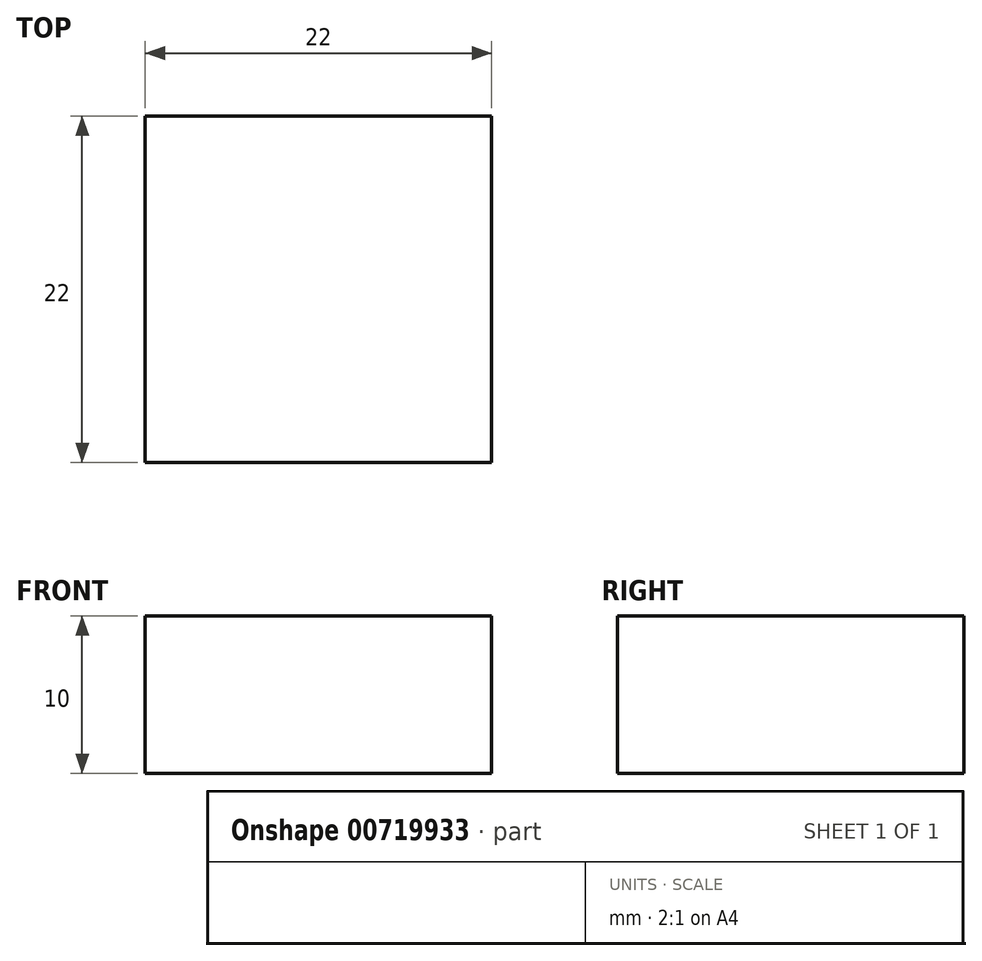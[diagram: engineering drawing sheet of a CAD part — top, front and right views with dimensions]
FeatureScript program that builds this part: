
annotation { "Feature Type Name" : "Feature", "Feature Type Description" : "" }
export const myFeature = defineFeature(function(context is Context, id is Id, definition is map)
    precondition{}
    {
        {
            var Q0;
            Q0=qCreatedBy(makeId("Top.planeOp"),FACE);
            var sketch = newSketch(context, id + "F0", { "sketchPlane" : qUnion([Q0])});
            skLineSegment(sketch, "E0.bottom", {"start": v(0, 0) * mm, "end": v(22, 0) * mm});
            skLineSegment(sketch, "E0.top", {"start": v(0, -22) * mm, "end": v(22, -22) * mm});
            skLineSegment(sketch, "E0.left", {"start": v(0, 0) * mm, "end": v(0, -22) * mm});
            skLineSegment(sketch, "E0.right", {"start": v(22, 0) * mm, "end": v(22, -22) * mm});
            skSolve(sketch);
        }
        {
            var Q0;
            Q0 = qSketchRegion(id + "F0", true);
            extrude(context, id + "F1", {"entities" : qUnion([Q0]), "depth" : 10 * mm, "offsetDistance" : 25 * mm});
        }
    });
